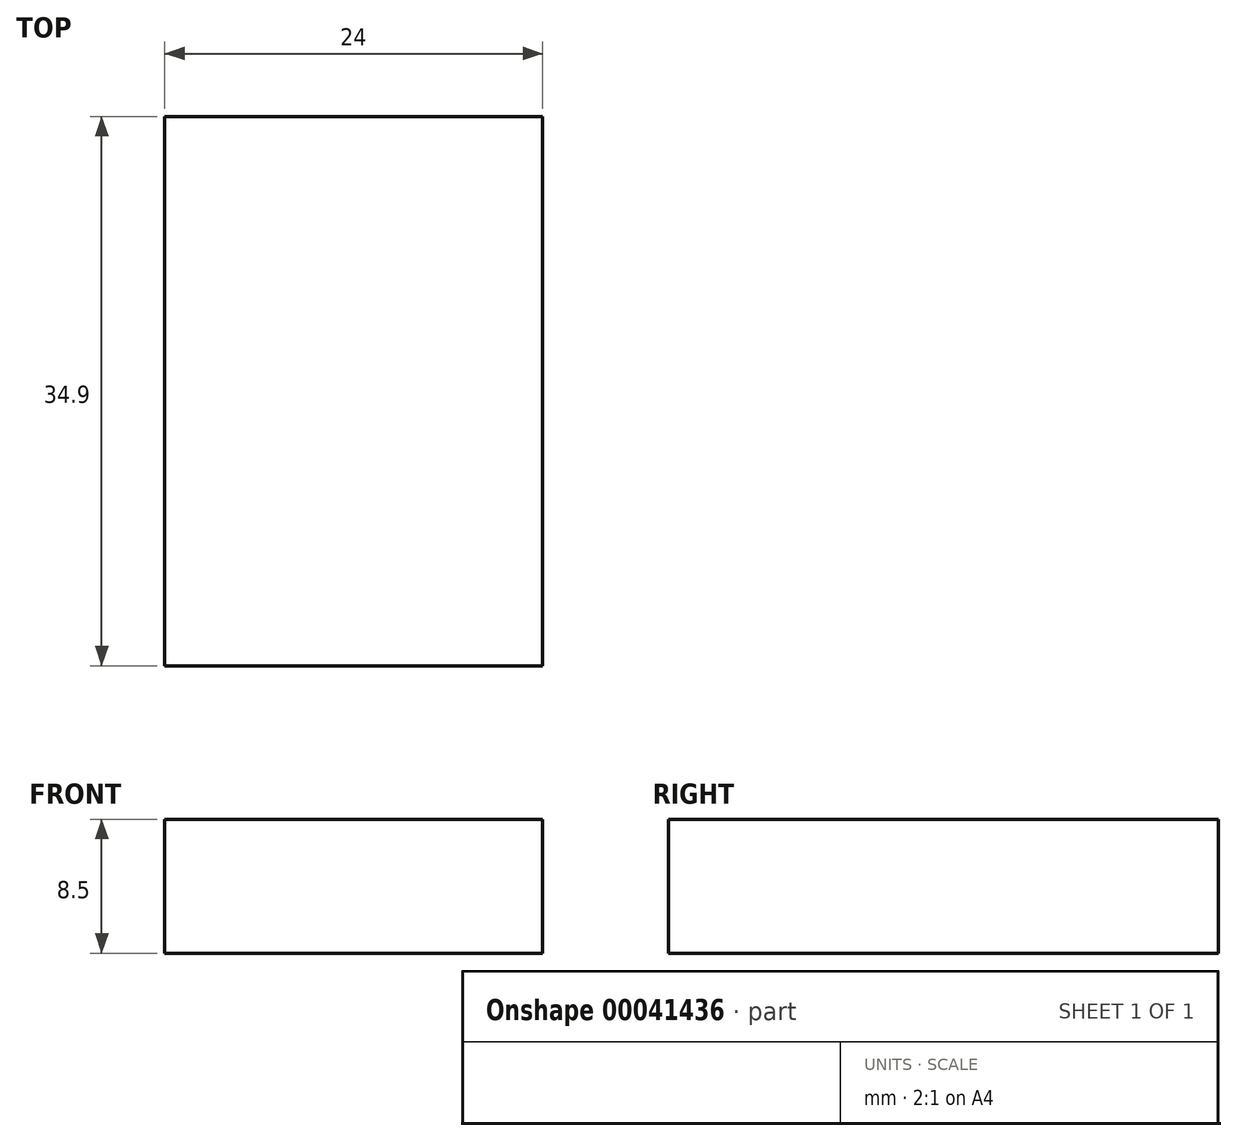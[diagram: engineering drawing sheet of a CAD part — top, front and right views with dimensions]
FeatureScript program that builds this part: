
annotation { "Feature Type Name" : "Feature", "Feature Type Description" : "" }
export const myFeature = defineFeature(function(context is Context, id is Id, definition is map)
    precondition{}
    {
        {
            var Q0;
            Q0=qCreatedBy(makeId("Top.planeOp"),FACE);
            var sketch = newSketch(context, id + "F0", { "sketchPlane" : qUnion([Q0])});
            skLineSegment(sketch, "E0.bottom", {"start": v(0, 0) * mm, "end": v(24, 0) * mm});
            skLineSegment(sketch, "E0.top", {"start": v(0, -34.9) * mm, "end": v(24, -34.9) * mm});
            skLineSegment(sketch, "E0.left", {"start": v(0, 0) * mm, "end": v(0, -34.9) * mm});
            skLineSegment(sketch, "E0.right", {"start": v(24, 0) * mm, "end": v(24, -34.9) * mm});
            skSolve(sketch);
        }
        {
            var Q0;
            Q0=makeQuery(id+"F0.imprint","IMPRINT",FACE,{"disambiguationData":[TD([[makeQuery(id+"F0.imprint","IMPRINT",EDGE,{"derivedFrom":sQuery(id+"F0.wireOp",EDGE,"E0.bottom")}),-1.0]])]});
            extrude(context, id + "F1", {"entities" : qUnion([Q0]), "depth" : 8.5 * mm});
        }
    });
